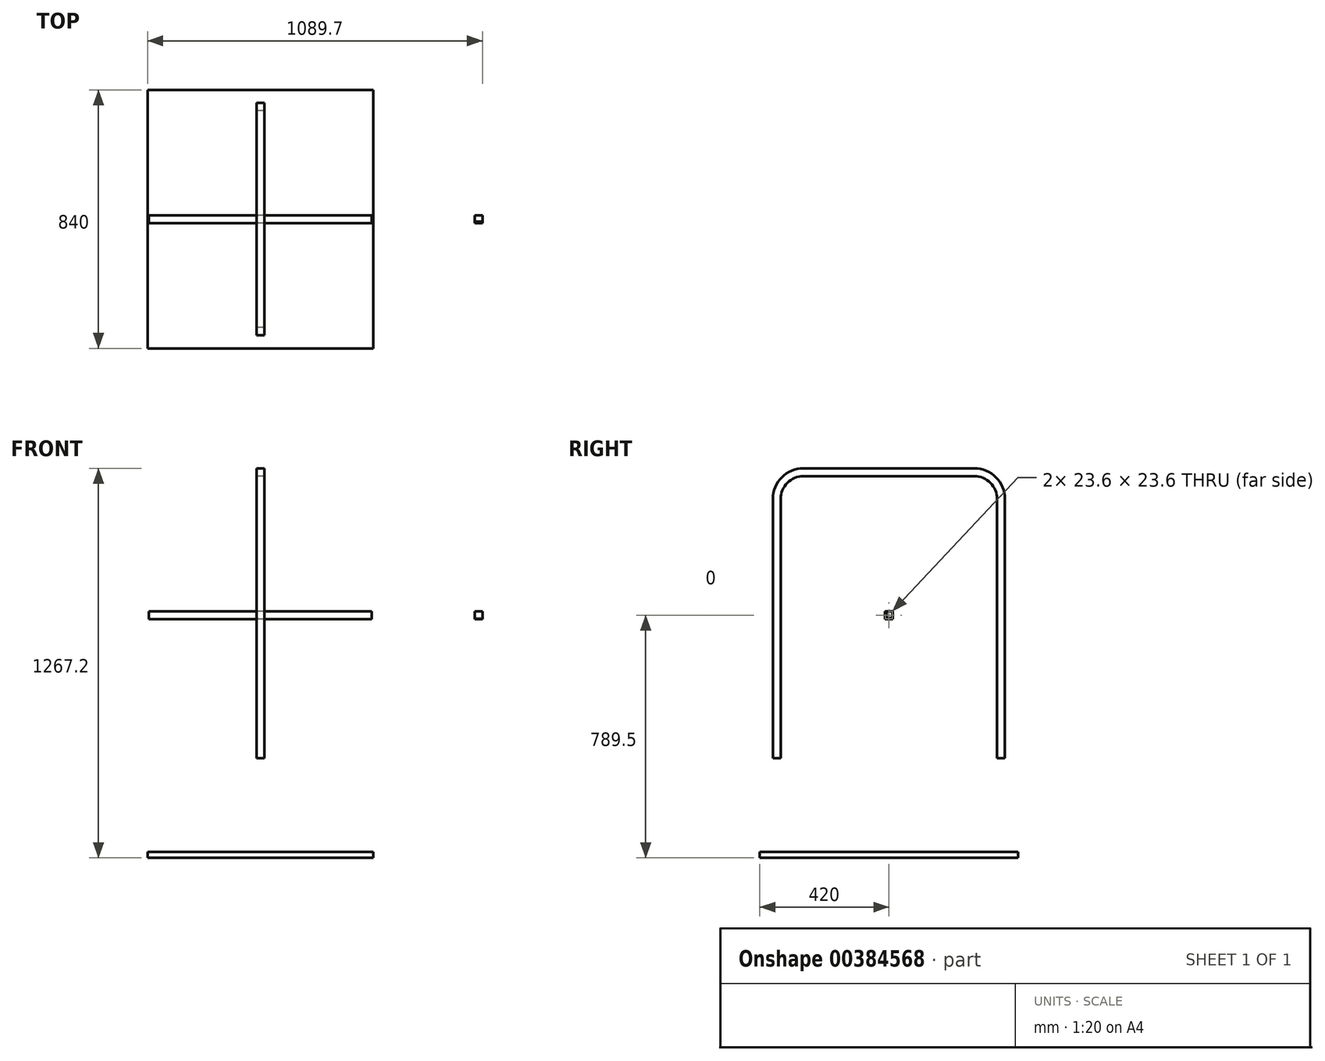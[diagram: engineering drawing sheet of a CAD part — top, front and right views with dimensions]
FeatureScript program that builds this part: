
annotation { "Feature Type Name" : "Feature", "Feature Type Description" : "" }
export const myFeature = defineFeature(function(context is Context, id is Id, definition is map)
    precondition{}
    {
        {
            var Q0;
            Q0=qCreatedBy(makeId("Right.planeOp"),FACE);
            var sketch = newSketch(context, id + "F0", { "sketchPlane" : qUnion([Q0])});
            skLineSegment(sketch, "E0.top", {"start": v(277.5, 465) * mm, "end": v(-277.5, 465) * mm, "construction": true});
            skLineSegment(sketch, "E0.left", {"start": v(365, -465) * mm, "end": v(365, 377.5) * mm, "construction": true});
            skLineSegment(sketch, "E0.right", {"start": v(-365, -465) * mm, "end": v(-365, 377.5) * mm, "construction": true});
            skPoint(sketch, "E0.middle", {"position": v(0, 0) * mm});
            skPoint(sketch, "E1.visualSharp", {"position": v(-365, 465) * mm});
            skArc(sketch, "E1.filletArc", {"start": v(-277.5, 465) * mm, "mid": v(-339.37, 439.37) * mm, "end": v(-365, 377.5) * mm, "construction": true});
            skPoint(sketch, "E2.visualSharp", {"position": v(365, 465) * mm});
            skArc(sketch, "E2.filletArc", {"start": v(365, 377.5) * mm, "mid": v(339.37, 439.37) * mm, "end": v(277.5, 465) * mm, "construction": true});
            skLineSegment(sketch, "E3.0", {"start": v(-377.7, -465) * mm, "end": v(-377.7, 377.5) * mm});
            skLineSegment(sketch, "E3.1", {"start": v(377.7, -465) * mm, "end": v(377.7, 377.5) * mm});
            skArc(sketch, "E3.2", {"start": v(377.7, 377.5) * mm, "mid": v(348.35, 448.35) * mm, "end": v(277.5, 477.7) * mm});
            skLineSegment(sketch, "E3.3", {"start": v(277.5, 477.7) * mm, "end": v(-277.5, 477.7) * mm});
            skArc(sketch, "E3.4", {"start": v(-277.5, 477.7) * mm, "mid": v(-348.35, 448.35) * mm, "end": v(-377.7, 377.5) * mm});
            skLineSegment(sketch, "E4.0", {"start": v(-352.3, -465) * mm, "end": v(-352.3, 377.5) * mm});
            skLineSegment(sketch, "E4.1", {"start": v(352.3, -465) * mm, "end": v(352.3, 377.5) * mm});
            skArc(sketch, "E4.2", {"start": v(352.3, 377.5) * mm, "mid": v(330.4, 430.4) * mm, "end": v(277.5, 452.3) * mm});
            skLineSegment(sketch, "E4.3", {"start": v(277.5, 452.3) * mm, "end": v(-277.5, 452.3) * mm});
            skArc(sketch, "E4.4", {"start": v(-277.5, 452.3) * mm, "mid": v(-330.4, 430.4) * mm, "end": v(-352.3, 377.5) * mm});
            skLineSegment(sketch, "E5", {"start": v(-377.7, -465) * mm, "end": v(-352.3, -465) * mm});
            skLineSegment(sketch, "E6", {"start": v(377.7, -465) * mm, "end": v(352.3, -465) * mm});
            skSolve(sketch);
        }
        {
            var Q0;
            Q0 = qSketchRegion(id + "F0", true);
            extrude(context, id + "F1", {"entities" : qUnion([Q0]), "endBound" : BoundingType.SYMMETRIC, "depth" : 25.4 * mm});
        }
        {
            var Q0;
            Q0=qCreatedBy(makeId("Right.planeOp"),FACE);
            var sketch = newSketch(context, id + "F2", { "sketchPlane" : qUnion([Q0])});
            skLineSegment(sketch, "E7.bottom", {"start": v(-12.7, -12.7) * mm, "end": v(12.7, -12.7) * mm});
            skLineSegment(sketch, "E7.top", {"start": v(-12.7, 12.7) * mm, "end": v(12.7, 12.7) * mm});
            skLineSegment(sketch, "E7.left", {"start": v(-12.7, -12.7) * mm, "end": v(-12.7, 12.7) * mm});
            skLineSegment(sketch, "E7.right", {"start": v(12.7, -12.7) * mm, "end": v(12.7, 12.7) * mm});
            skPoint(sketch, "E7.middle", {"position": v(0, 0) * mm});
            skLineSegment(sketch, "E8.bottom", {"start": v(-11.8, -11.8) * mm, "end": v(11.8, -11.8) * mm});
            skLineSegment(sketch, "E8.top", {"start": v(-11.8, 11.8) * mm, "end": v(11.8, 11.8) * mm});
            skLineSegment(sketch, "E8.left", {"start": v(-11.8, -11.8) * mm, "end": v(-11.8, 11.8) * mm});
            skLineSegment(sketch, "E8.right", {"start": v(11.8, -11.8) * mm, "end": v(11.8, 11.8) * mm});
            skSolve(sketch);
        }
        {
            var Q0;
            Q0 = qSketchRegion(id + "F2", true);
            extrude(context, id + "F3", {"entities" : qUnion([Q0]), "endBound" : BoundingType.SYMMETRIC, "depth" : (750 - 25.4) * mm});
        }
        {
            var Q0;
            Q0=qCreatedBy(makeId("Right.planeOp"),FACE);
            cPlane(context, id + "F4", {"entities" : qUnion([Q0]), "cplaneType" : CPlaneType.OFFSET, "offset" : 710 * mm, "width" : 150 * mm, "height" : 150 * mm});
        }
        {
            var Q0;
            Q0=qCreatedBy(id+"F4.planeOp",FACE);
            var sketch = newSketch(context, id + "F5", { "sketchPlane" : qUnion([Q0])});
            skLineSegment(sketch, "E9.bottom", {"start": v(12.7, -12.7) * mm, "end": v(-12.7, -12.7) * mm});
            skLineSegment(sketch, "E9.top", {"start": v(-7.94, 12.7) * mm, "end": v(-12.7, 12.7) * mm});
            skLineSegment(sketch, "E9.left", {"start": v(12.7, -12.7) * mm, "end": v(12.7, -9.36) * mm});
            skLineSegment(sketch, "E9.right", {"start": v(-12.7, -12.7) * mm, "end": v(-12.7, 12.7) * mm});
            skLineSegment(sketch, "E10.bottom", {"start": v(-7.94, -9.36) * mm, "end": v(7.94, -9.36) * mm});
            skLineSegment(sketch, "E10.right", {"start": v(-7.94, -9.36) * mm, "end": v(-7.94, 9.36) * mm});
            skPoint(sketch, "E10.middle", {"position": v(0, 0) * mm});
            skLineSegment(sketch, "E11", {"start": v(-7.94, 9.36) * mm, "end": v(-7.94, 12.7) * mm});
            skLineSegment(sketch, "E12", {"start": v(7.94, -9.36) * mm, "end": v(12.7, -9.36) * mm});
            skSolve(sketch);
        }
        {
            var Q0;
            Q0 = qSketchRegion(id + "F5", true);
            extrude(context, id + "F6", {"entities" : qUnion([Q0]), "endBound" : BoundingType.SYMMETRIC, "depth" : 25.4 * mm});
        }
        {
            var Q0;
            Q0=qCreatedBy(makeId("Top.planeOp"),FACE);
            cPlane(context, id + "F7", {"entities" : qUnion([Q0]), "cplaneType" : CPlaneType.OFFSET, "offset" : 780 * mm, "oppositeDirection" : true, "width" : 150 * mm, "height" : 150 * mm});
        }
        {
            var Q0;
            Q0=qCreatedBy(id+"F7.planeOp",FACE);
            var sketch = newSketch(context, id + "F8", { "sketchPlane" : qUnion([Q0])});
            skLineSegment(sketch, "E13.bottom", {"start": v(367, 420) * mm, "end": v(-367, 420) * mm});
            skLineSegment(sketch, "E13.top", {"start": v(367, -420) * mm, "end": v(-367, -420) * mm});
            skLineSegment(sketch, "E13.left", {"start": v(367, 420) * mm, "end": v(367, -420) * mm});
            skLineSegment(sketch, "E13.right", {"start": v(-367, 420) * mm, "end": v(-367, -420) * mm});
            skPoint(sketch, "E13.middle", {"position": v(0, 0) * mm});
            skSolve(sketch);
        }
        {
            var Q0;
            Q0=makeQuery(id+"F8.imprint","IMPRINT",FACE,{"disambiguationData":[TD([[makeQuery(id+"F8.imprint","IMPRINT",EDGE,{"derivedFrom":sQuery(id+"F8.wireOp",EDGE,"E13.bottom")}),1.0]])]});
            extrude(context, id + "F9", {"entities" : qUnion([Q0]), "endBound" : BoundingType.SYMMETRIC, "depth" : 19 * mm});
        }
    });
